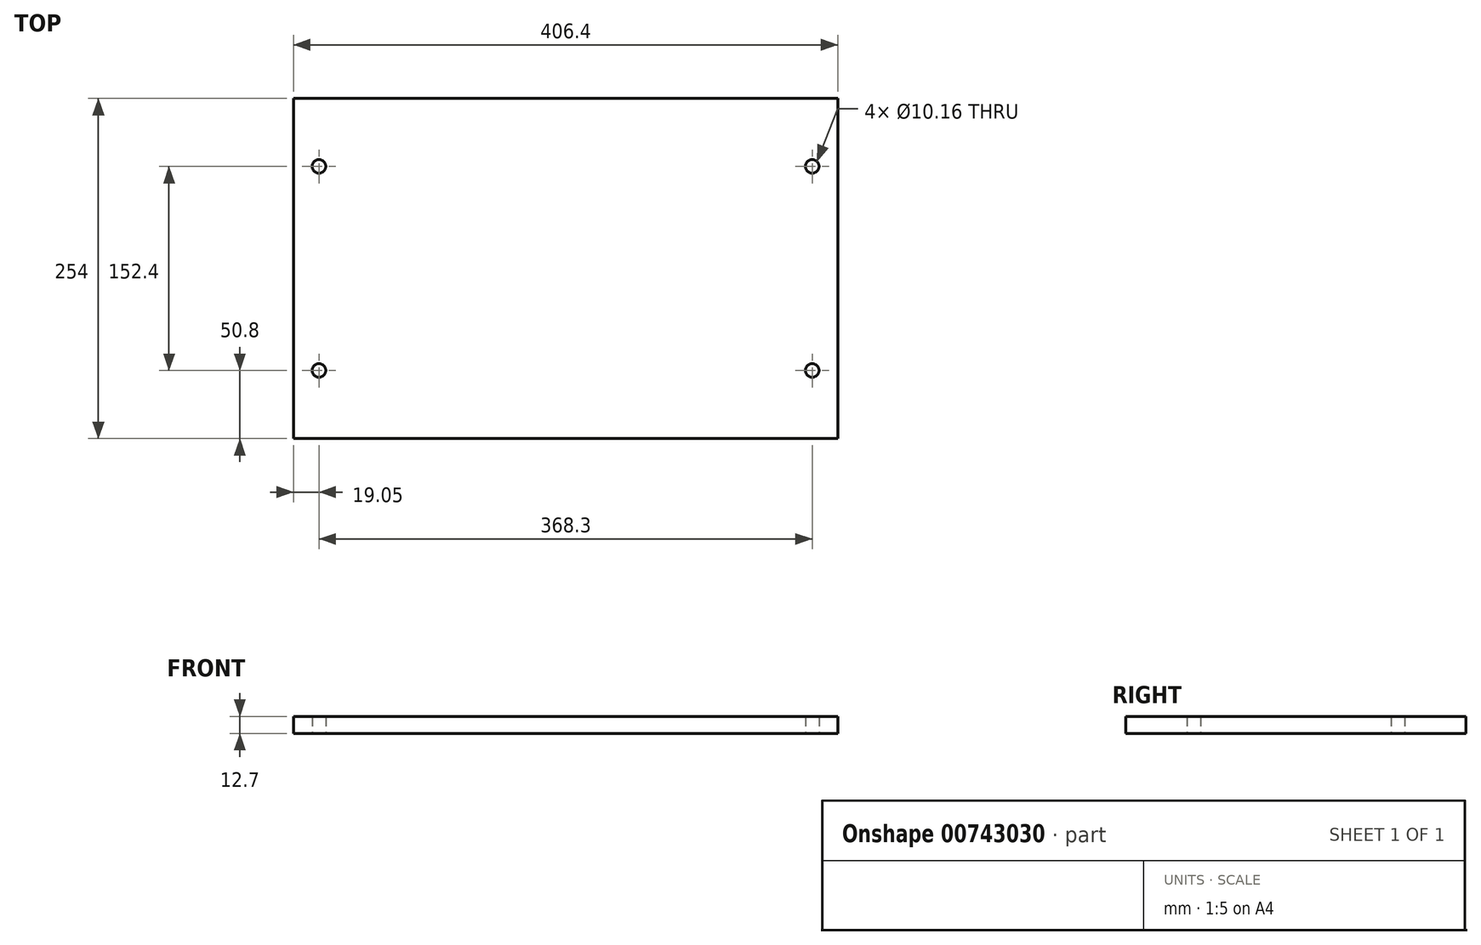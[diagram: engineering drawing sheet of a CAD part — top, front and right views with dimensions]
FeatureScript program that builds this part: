
annotation { "Feature Type Name" : "Feature", "Feature Type Description" : "" }
export const myFeature = defineFeature(function(context is Context, id is Id, definition is map)
    precondition{}
    {
        {
            var Q0;
            Q0=qCreatedBy(makeId("Top.planeOp"),FACE);
            var sketch = newSketch(context, id + "F0", { "sketchPlane" : qUnion([Q0])});
            skLineSegment(sketch, "E0.bottom", {"start": v(-203.2, -127) * mm, "end": v(203.2, -127) * mm});
            skLineSegment(sketch, "E0.top", {"start": v(-203.2, 127) * mm, "end": v(203.2, 127) * mm});
            skLineSegment(sketch, "E0.left", {"start": v(-203.2, -127) * mm, "end": v(-203.2, 127) * mm});
            skLineSegment(sketch, "E0.right", {"start": v(203.2, -127) * mm, "end": v(203.2, 127) * mm});
            skPoint(sketch, "E0.middle", {"position": v(0, 0) * mm});
            skSolve(sketch);
        }
        {
            var Q0;
            Q0=makeQuery(id+"F0.imprint","IMPRINT",FACE,{"disambiguationData":[TD([[makeQuery(id+"F0.imprint","IMPRINT",EDGE,{"derivedFrom":sQuery(id+"F0.wireOp",EDGE,"E0.bottom")}),1.0]])]});
            extrude(context, id + "F1", {"entities" : qUnion([Q0]), "depth" : 12.7 * mm, "offsetDistance" : 25.4 * mm, "symmetric" : true});
        }
        {
            var Q0;
            Q0=makeQuery(id+"F1.opExtrude","CAP_FACE",FACE,{"disambiguationData":[OSD([sQuery(id+"F0.wireOp",EDGE,"E0.bottom"),sQuery(id+"F0.wireOp",EDGE,"E0.top"),sQuery(id+"F0.wireOp",EDGE,"E0.left"),sQuery(id+"F0.wireOp",EDGE,"E0.right")])],"isStart":false});
            var sketch = newSketch(context, id + "F2", { "sketchPlane" : qUnion([Q0])});
            skPoint(sketch, "E1", {"position": v(-184.15, 76.2) * mm});
            skLineSegment(sketch, "E2", {"start": v(-203.2, 0) * mm, "end": v(203.2, 0) * mm, "construction": true});
            skLineSegment(sketch, "E3", {"start": v(0, 127) * mm, "end": v(0, -127) * mm, "construction": true});
            skPoint(sketch, "E4.MirrorP", {"position": v(184.15, 76.2) * mm});
            skPoint(sketch, "E5.MirrorP", {"position": v(184.15, -76.2) * mm});
            skPoint(sketch, "E6.MirrorP", {"position": v(-184.15, -76.2) * mm});
            skSolve(sketch);
        }
        {
            var Q0;
            Q0=sQuery(id+"F2.wireOp",VERTEX,"E1");
            var Q1;
            Q1=sQuery(id+"F2.wireOp",VERTEX,"E4.MirrorP");
            var Q2;
            Q2=sQuery(id+"F2.wireOp",VERTEX,"E5.MirrorP");
            var Q3;
            Q3=sQuery(id+"F2.wireOp",VERTEX,"E6.MirrorP");
            var Q4;
            Q4=makeQuery(id+"F1.opExtrude","SWEPT_BODY",BODY,{"disambiguationData":[OSD([sQuery(id+"F0.wireOp",EDGE,"E0.bottom"),sQuery(id+"F0.wireOp",EDGE,"E0.top"),sQuery(id+"F0.wireOp",EDGE,"E0.left"),sQuery(id+"F0.wireOp",EDGE,"E0.right")])]});
            hole(context, id + "F3", {"style" : HoleStyle.SIMPLE, "endStyle" : HoleEndStyle.THROUGH, "holeDiameter" : 10.16 * mm, "majorDiameter" : 6.35 * mm, "isTappedThrough" : true, "tappedDepth" : 12.7 * mm, "tapClearance" : 3, "locations" : qUnion([Q0, Q1, Q2, Q3]), "scope" : qUnion([Q4])});
        }
    });
